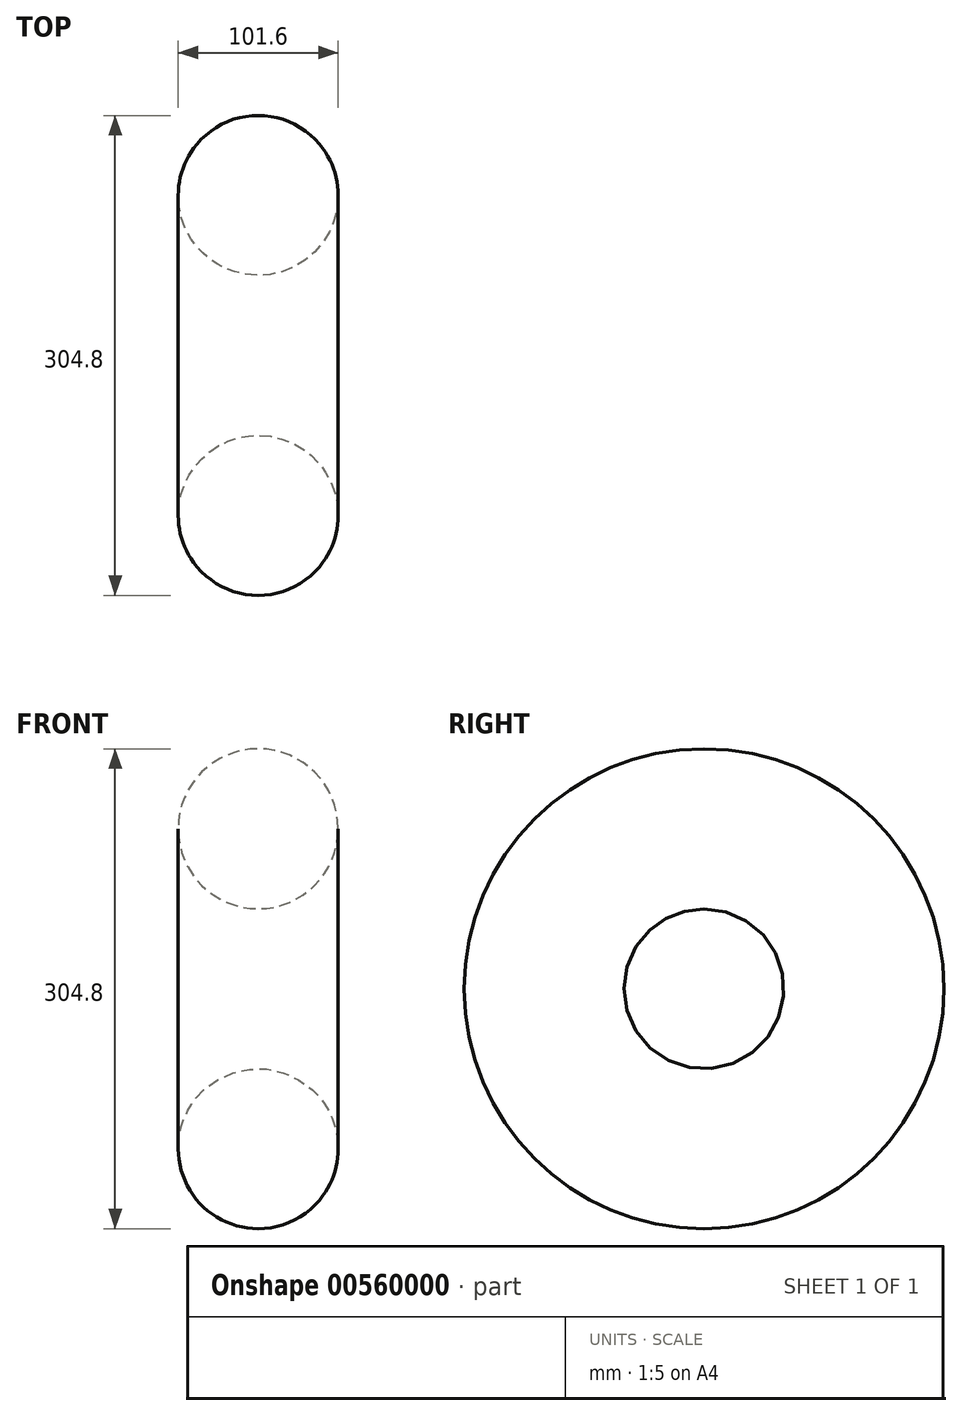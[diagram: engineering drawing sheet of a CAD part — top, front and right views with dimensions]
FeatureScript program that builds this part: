
annotation { "Feature Type Name" : "Feature", "Feature Type Description" : "" }
export const myFeature = defineFeature(function(context is Context, id is Id, definition is map)
    precondition{}
    {
        {
            var Q0;
            Q0=qCreatedBy(makeId("Front.planeOp"),FACE);
            var sketch = newSketch(context, id + "F0", { "sketchPlane" : qUnion([Q0])});
            skCircle(sketch, "E0", {"center": v(0, -101.6) * mm, "radius": 50.8 * mm});
            skLineSegment(sketch, "E1", {"start": v(0, 0) * mm, "end": v(55.82, 0) * mm, "construction": true});
            skSolve(sketch);
        }
        {
            var Q0;
            Q0=makeQuery(id+"F0.imprint","IMPRINT",FACE,{"disambiguationData":[TD([[makeQuery(id+"F0.imprint","IMPRINT",EDGE,{"derivedFrom":sQuery(id+"F0.wireOp",EDGE,"E0")}),1.0]])]});
            var Q1;
            Q1=sQuery(id+"F0.wireOp",EDGE,"E1");
            revolve(context, id + "F1", {"entities" : qUnion([Q0]), "axis" : qUnion([Q1]), "revolveType" : RevolveType.FULL});
        }
    });
